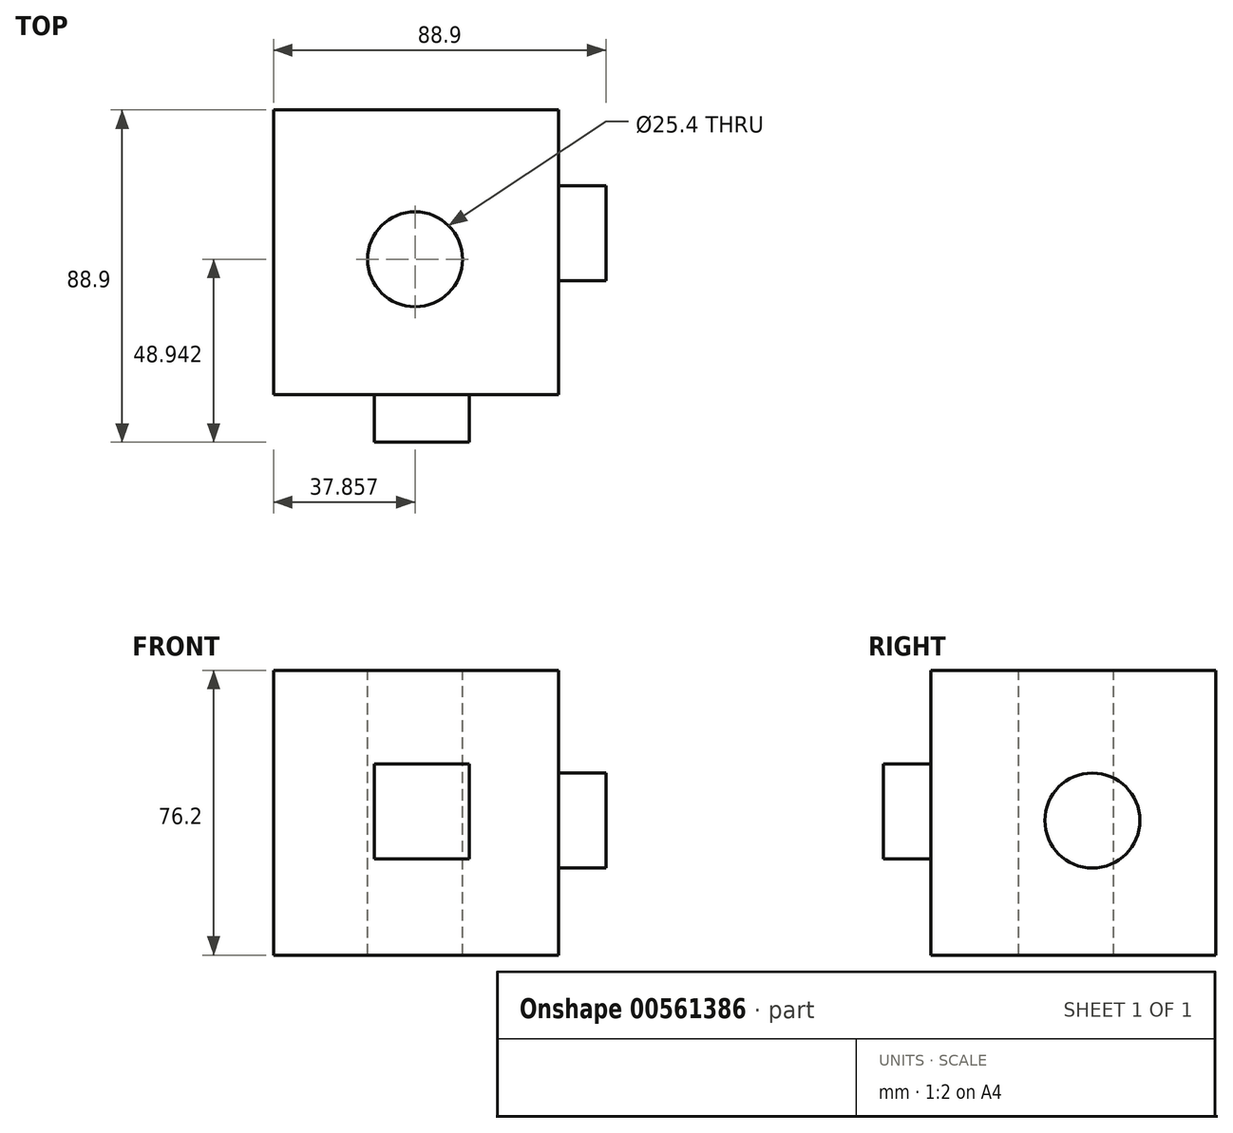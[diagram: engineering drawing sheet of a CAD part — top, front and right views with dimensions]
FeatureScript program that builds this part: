
annotation { "Feature Type Name" : "Feature", "Feature Type Description" : "" }
export const myFeature = defineFeature(function(context is Context, id is Id, definition is map)
    precondition{}
    {
        {
            var Q0;
            Q0=qCreatedBy(makeId("Front.planeOp"),FACE);
            var sketch = newSketch(context, id + "F0", { "sketchPlane" : qUnion([Q0])});
            skLineSegment(sketch, "E0.bottom", {"start": v(0, 0) * mm, "end": v(76.2, 0) * mm});
            skLineSegment(sketch, "E0.top", {"start": v(0, 76.2) * mm, "end": v(76.2, 76.2) * mm});
            skLineSegment(sketch, "E0.left", {"start": v(0, 0) * mm, "end": v(0, 76.2) * mm});
            skLineSegment(sketch, "E0.right", {"start": v(76.2, 0) * mm, "end": v(76.2, 76.2) * mm});
            skSolve(sketch);
        }
        {
            var Q0;
            Q0=makeQuery(id+"F0.imprint","IMPRINT",FACE,{"disambiguationData":[TD([[makeQuery(id+"F0.imprint","IMPRINT",EDGE,{"derivedFrom":sQuery(id+"F0.wireOp",EDGE,"E0.bottom")}),1.0]])]});
            extrude(context, id + "F1", {"entities" : qUnion([Q0]), "depth" : 76.2 * mm, "offsetDistance" : 25.4 * mm});
        }
        {
            var Q0;
            Q0=makeQuery(id+"F1.opExtrude","SWEPT_FACE",FACE,{"disambiguationData":[OSD([sQuery(id+"F0.wireOp",EDGE,"E0.top")])]});
            var sketch = newSketch(context, id + "F2", { "sketchPlane" : qUnion([Q0])});
            skPoint(sketch, "E1", {"position": v(37.86, -39.96) * mm});
            skSolve(sketch);
        }
        {
            var Q0;
            Q0=sQuery(id+"F2.wireOp",VERTEX,"E1");
            var Q1;
            Q1=makeQuery(id+"F1.opExtrude","SWEPT_BODY",BODY,{"disambiguationData":[OSD([sQuery(id+"F0.wireOp",EDGE,"E0.bottom"),sQuery(id+"F0.wireOp",EDGE,"E0.top"),sQuery(id+"F0.wireOp",EDGE,"E0.left"),sQuery(id+"F0.wireOp",EDGE,"E0.right")])]});
            hole(context, id + "F3", {"style" : HoleStyle.SIMPLE, "endStyle" : HoleEndStyle.THROUGH, "holeDiameter" : 25.4 * mm, "isTappedThrough" : true, "tappedDepth" : 12.7 * mm, "tapClearance" : 3, "locations" : qUnion([Q0]), "scope" : qUnion([Q1])});
        }
        {
            var Q0;
            Q0=makeQuery(id+"F1.opExtrude","CAP_FACE",FACE,{"disambiguationData":[OSD([sQuery(id+"F0.wireOp",EDGE,"E0.bottom"),sQuery(id+"F0.wireOp",EDGE,"E0.top"),sQuery(id+"F0.wireOp",EDGE,"E0.left"),sQuery(id+"F0.wireOp",EDGE,"E0.right")])],"isStart":false});
            var sketch = newSketch(context, id + "F4", { "sketchPlane" : qUnion([Q0])});
            skLineSegment(sketch, "E2.bottom", {"start": v(26.99, 51.18) * mm, "end": v(52.39, 51.18) * mm});
            skLineSegment(sketch, "E2.top", {"start": v(26.99, 25.78) * mm, "end": v(52.39, 25.78) * mm});
            skLineSegment(sketch, "E2.left", {"start": v(26.99, 51.18) * mm, "end": v(26.99, 25.78) * mm});
            skLineSegment(sketch, "E2.right", {"start": v(52.39, 51.18) * mm, "end": v(52.39, 25.78) * mm});
            skSolve(sketch);
        }
        {
            var Q0;
            Q0=makeQuery(id+"F4.imprint","IMPRINT",FACE,{"disambiguationData":[TD([[makeQuery(id+"F4.imprint","IMPRINT",EDGE,{"derivedFrom":sQuery(id+"F4.wireOp",EDGE,"E2.bottom")}),-1.0]])]});
            extrude(context, id + "F5", {"entities" : qUnion([Q0]), "operationType" : NewBodyOperationType.ADD, "depth" : 12.7 * mm, "offsetDistance" : 25.4 * mm});
        }
        {
            var Q0;
            Q0=makeQuery(id+"F1.opExtrude","SWEPT_FACE",FACE,{"disambiguationData":[OSD([sQuery(id+"F0.wireOp",EDGE,"E0.right")])]});
            var sketch = newSketch(context, id + "F6", { "sketchPlane" : qUnion([Q0])});
            skCircle(sketch, "E3", {"center": v(-33, 36) * mm, "radius": 12.7 * mm});
            skSolve(sketch);
        }
        {
            var Q0;
            Q0=makeQuery(id+"F6.imprint","IMPRINT",FACE,{"disambiguationData":[TD([[makeQuery(id+"F6.imprint","IMPRINT",EDGE,{"derivedFrom":sQuery(id+"F6.wireOp",EDGE,"E3")}),1.0]])]});
            extrude(context, id + "F7", {"entities" : qUnion([Q0]), "operationType" : NewBodyOperationType.ADD, "depth" : 12.7 * mm, "offsetDistance" : 25.4 * mm});
        }
    });
